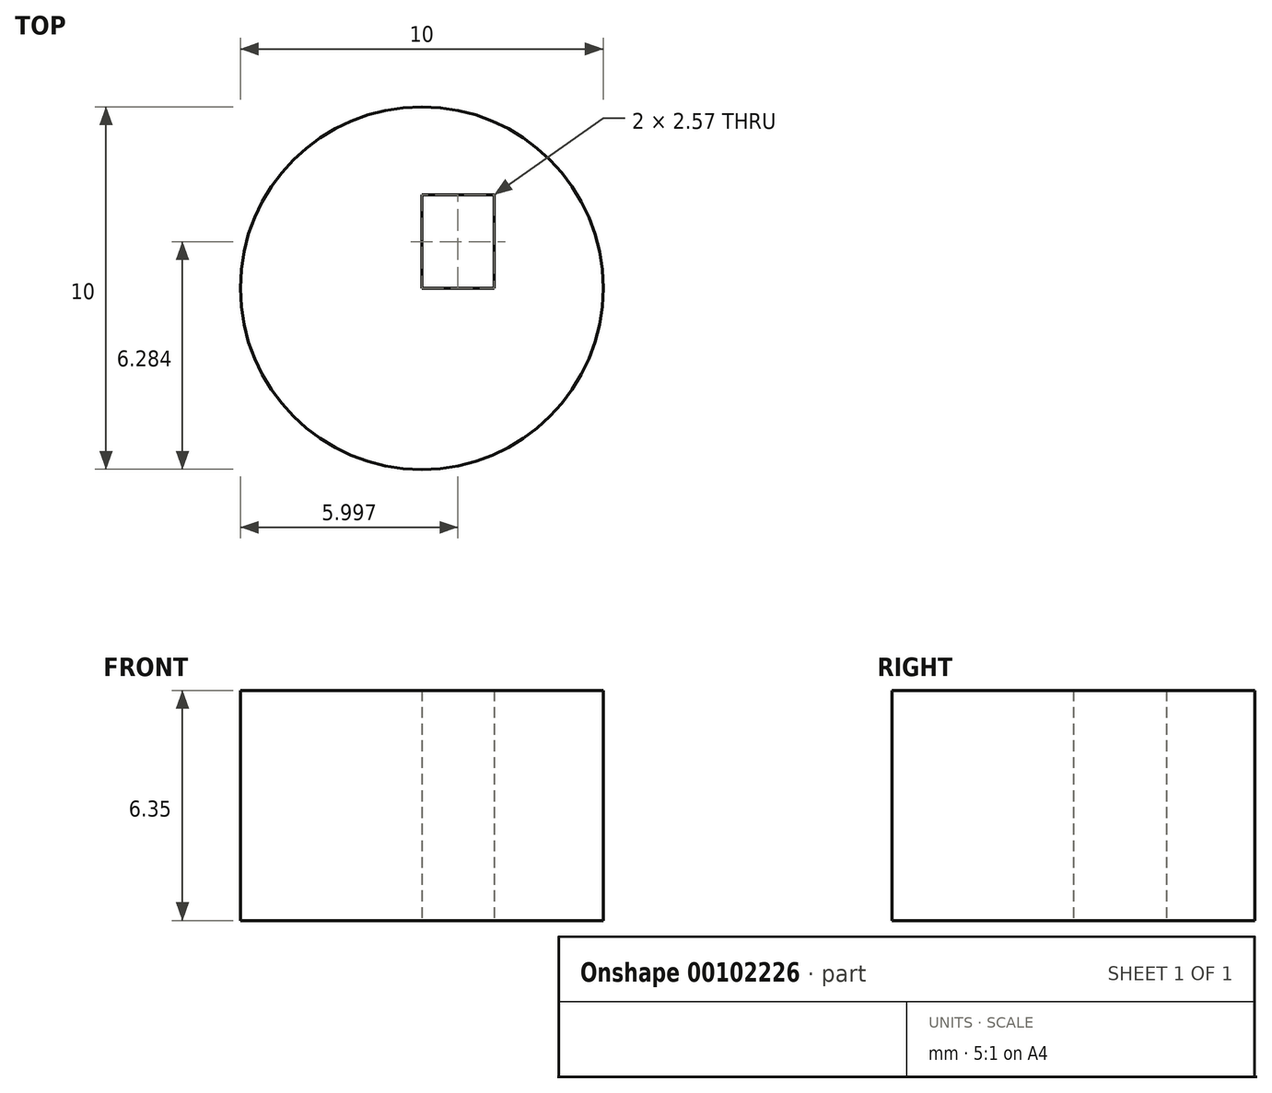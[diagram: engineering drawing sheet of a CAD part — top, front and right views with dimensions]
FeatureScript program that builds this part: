
annotation { "Feature Type Name" : "Feature", "Feature Type Description" : "" }
export const myFeature = defineFeature(function(context is Context, id is Id, definition is map)
    precondition{}
    {
        {
            var Q0;
            Q0=qCreatedBy(makeId("Top.planeOp"),FACE);
            var sketch = newSketch(context, id + "F0", { "sketchPlane" : qUnion([Q0])});
            skCircle(sketch, "E0", {"center": v(-36.51, 20.68) * mm, "radius": 5 * mm});
            skLineSegment(sketch, "E1.bottom", {"start": v(-36.51, 23.25) * mm, "end": v(-34.51, 23.25) * mm});
            skLineSegment(sketch, "E1.top", {"start": v(-36.51, 20.68) * mm, "end": v(-34.51, 20.68) * mm});
            skLineSegment(sketch, "E1.left", {"start": v(-36.51, 23.25) * mm, "end": v(-36.51, 20.68) * mm});
            skLineSegment(sketch, "E1.right", {"start": v(-34.51, 23.25) * mm, "end": v(-34.51, 20.68) * mm});
            skSolve(sketch);
        }
        {
            var Q0;
            Q0=makeQuery(id+"F0.imprint","IMPRINT",FACE,{"disambiguationData":[TD([[makeQuery(id+"F0.imprint","IMPRINT",EDGE,{"derivedFrom":sQuery(id+"F0.wireOp",EDGE,"E0")}),1.0]])]});
            var Q1;
            Q1=sQuery(id+"F0.wireOp",EDGE,"E0");
            extrude(context, id + "F1", {"entities" : qUnion([Q0]), "surfaceEntities" : qUnion([Q1]), "depth" : 6.35 * mm});
        }
    });
